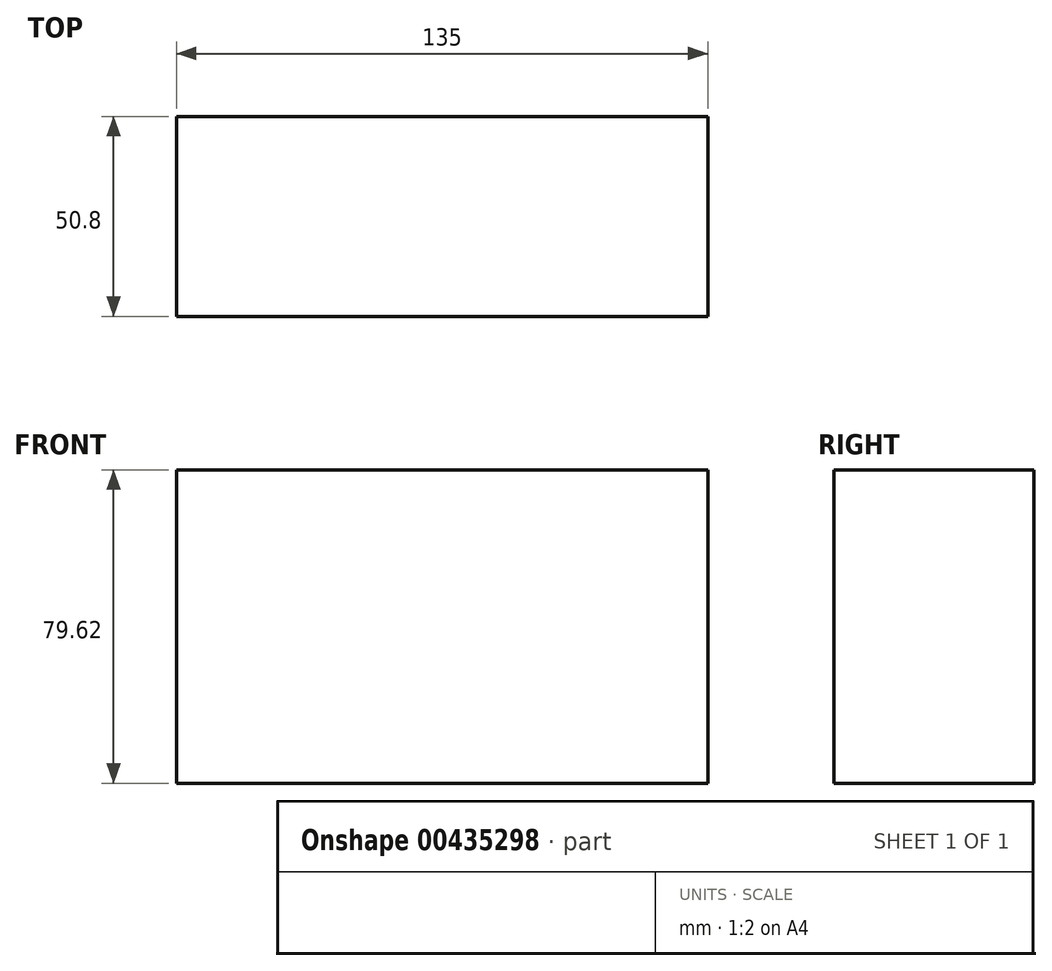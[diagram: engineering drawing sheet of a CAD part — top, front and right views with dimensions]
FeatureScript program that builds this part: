
annotation { "Feature Type Name" : "Feature", "Feature Type Description" : "" }
export const myFeature = defineFeature(function(context is Context, id is Id, definition is map)
    precondition{}
    {
        {
            var Q0;
            Q0=qCreatedBy(makeId("Front.planeOp"),FACE);
            var sketch = newSketch(context, id + "F0", { "sketchPlane" : qUnion([Q0])});
            skLineSegment(sketch, "E0.bottom", {"start": v(-68.17, 46.97) * mm, "end": v(66.83, 46.97) * mm});
            skLineSegment(sketch, "E0.top", {"start": v(-68.17, -32.65) * mm, "end": v(66.83, -32.65) * mm});
            skLineSegment(sketch, "E0.left", {"start": v(-68.17, 46.97) * mm, "end": v(-68.17, -32.65) * mm});
            skLineSegment(sketch, "E0.right", {"start": v(66.83, 46.97) * mm, "end": v(66.83, -32.65) * mm});
            skSolve(sketch);
        }
        {
            var Q0;
            Q0=makeQuery(id+"F0.imprint","IMPRINT",FACE,{"disambiguationData":[TD([[makeQuery(id+"F0.imprint","IMPRINT",EDGE,{"derivedFrom":sQuery(id+"F0.wireOp",EDGE,"E0.bottom")}),-1.0]])]});
            extrude(context, id + "F1", {"entities" : qUnion([Q0]), "depth" : 25.4 * mm});
        }
        {
            var Q0;
            Q0=qCreatedBy(makeId("Front.planeOp"),FACE);
            var sketch = newSketch(context, id + "F2", { "sketchPlane" : qUnion([Q0])});
            skLineSegment(sketch, "E1.bottom", {"start": v(-59.2, 29.6) * mm, "end": v(-30.74, 29.6) * mm});
            skLineSegment(sketch, "E1.top", {"start": v(-59.2, 8.4) * mm, "end": v(-30.74, 8.4) * mm});
            skLineSegment(sketch, "E1.left", {"start": v(-59.2, 29.6) * mm, "end": v(-59.2, 8.4) * mm});
            skLineSegment(sketch, "E1.right", {"start": v(-30.74, 29.6) * mm, "end": v(-30.74, 8.4) * mm});
            skCircle(sketch, "E2", {"center": v(23.87, 11.84) * mm, "radius": 12.45 * mm});
            skSolve(sketch);
        }
        {
            var Q0;
            Q0=makeQuery(id+"F1.opExtrude","CAP_FACE",FACE,{"disambiguationData":[OSD([sQuery(id+"F0.wireOp",EDGE,"E0.bottom"),sQuery(id+"F0.wireOp",EDGE,"E0.top"),sQuery(id+"F0.wireOp",EDGE,"E0.left"),sQuery(id+"F0.wireOp",EDGE,"E0.right")])],"isStart":false});
            var Q1;
            Q1=makeQuery(id+"F2.imprint","IMPRINT",FACE,{"disambiguationData":[TD([[makeQuery(id+"F2.imprint","IMPRINT",EDGE,{"derivedFrom":sQuery(id+"F2.wireOp",EDGE,"E1.bottom")}),-1.0]])]});
            var Q2;
            Q2=makeQuery(id+"F1.opExtrude","CAP_FACE",FACE,{"disambiguationData":[OSD([sQuery(id+"F0.wireOp",EDGE,"E0.bottom"),sQuery(id+"F0.wireOp",EDGE,"E0.top"),sQuery(id+"F0.wireOp",EDGE,"E0.left"),sQuery(id+"F0.wireOp",EDGE,"E0.right")])],"isStart":true});
            extrude(context, id + "F3", {"entities" : qUnion([Q0, Q1, Q2]), "operationType" : NewBodyOperationType.ADD, "depth" : 25.4 * mm});
        }
    });
